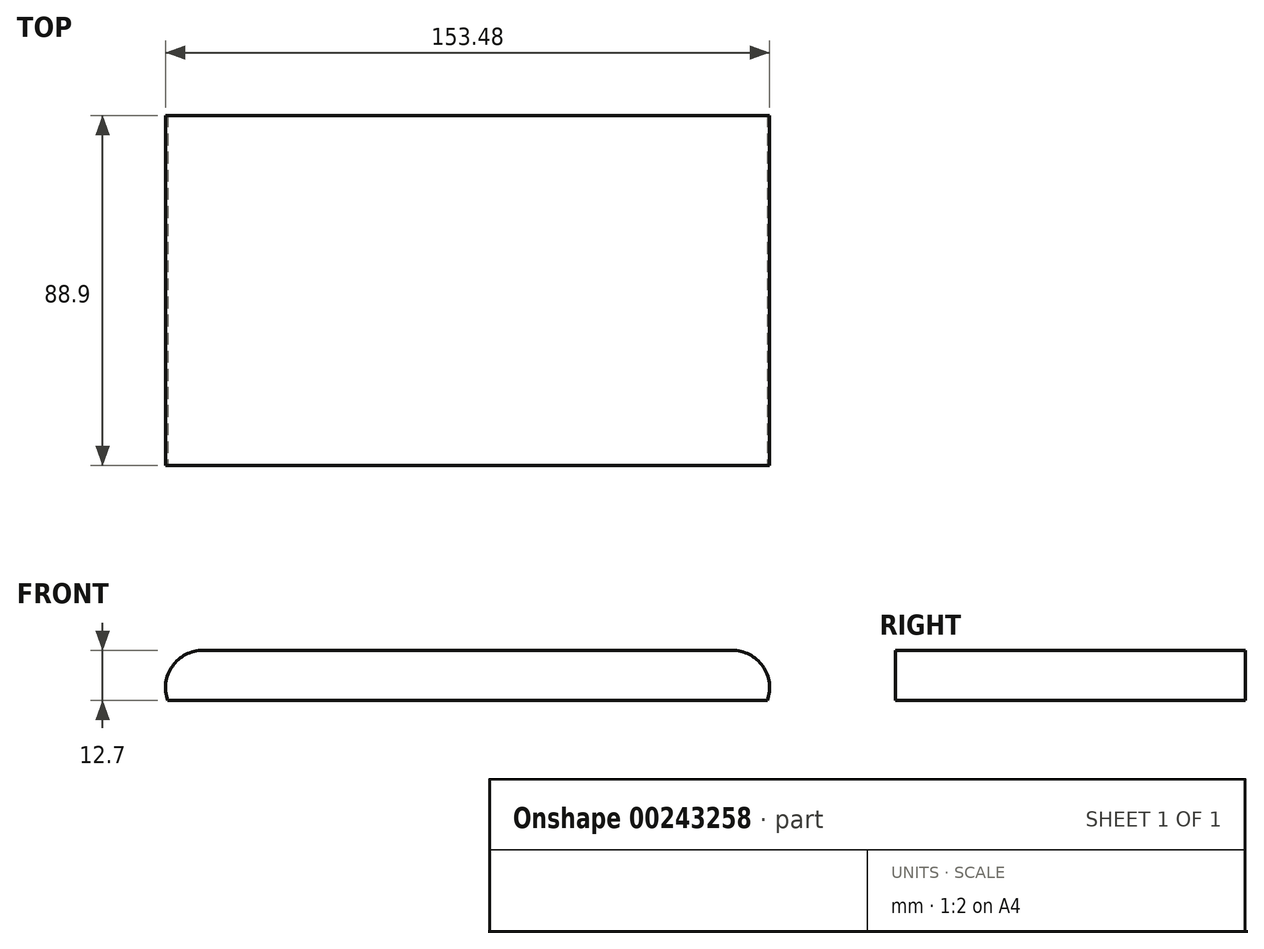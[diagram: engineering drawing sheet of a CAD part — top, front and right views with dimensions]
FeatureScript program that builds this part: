
annotation { "Feature Type Name" : "Feature", "Feature Type Description" : "" }
export const myFeature = defineFeature(function(context is Context, id is Id, definition is map)
    precondition{}
    {
        {
            var Q0;
            Q0=qCreatedBy(makeId("Front.planeOp"),FACE);
            var sketch = newSketch(context, id + "F0", { "sketchPlane" : qUnion([Q0])});
            skLineSegment(sketch, "E0", {"start": v(0, 0) * mm, "end": v(152.4, 0) * mm});
            skLineSegment(sketch, "E1", {"start": v(8.98, 12.7) * mm, "end": v(143.42, 12.7) * mm});
            skArc(sketch, "E2", {"start": v(8.98, 12.7) * mm, "mid": v(1.2, 8.67) * mm, "end": v(0, 0) * mm});
            skArc(sketch, "E3", {"start": v(152.4, 0) * mm, "mid": v(151.2, 8.67) * mm, "end": v(143.42, 12.7) * mm});
            skSolve(sketch);
        }
        {
            var Q0;
            Q0=makeQuery(id+"F0.imprint","IMPRINT",FACE,{"disambiguationData":[TD([[makeQuery(id+"F0.imprint","IMPRINT",EDGE,{"derivedFrom":sQuery(id+"F0.wireOp",EDGE,"E0")}),1.0]])]});
            extrude(context, id + "F1", {"entities" : qUnion([Q0]), "oppositeDirection" : true, "depth" : 88.9 * mm});
        }
    });
